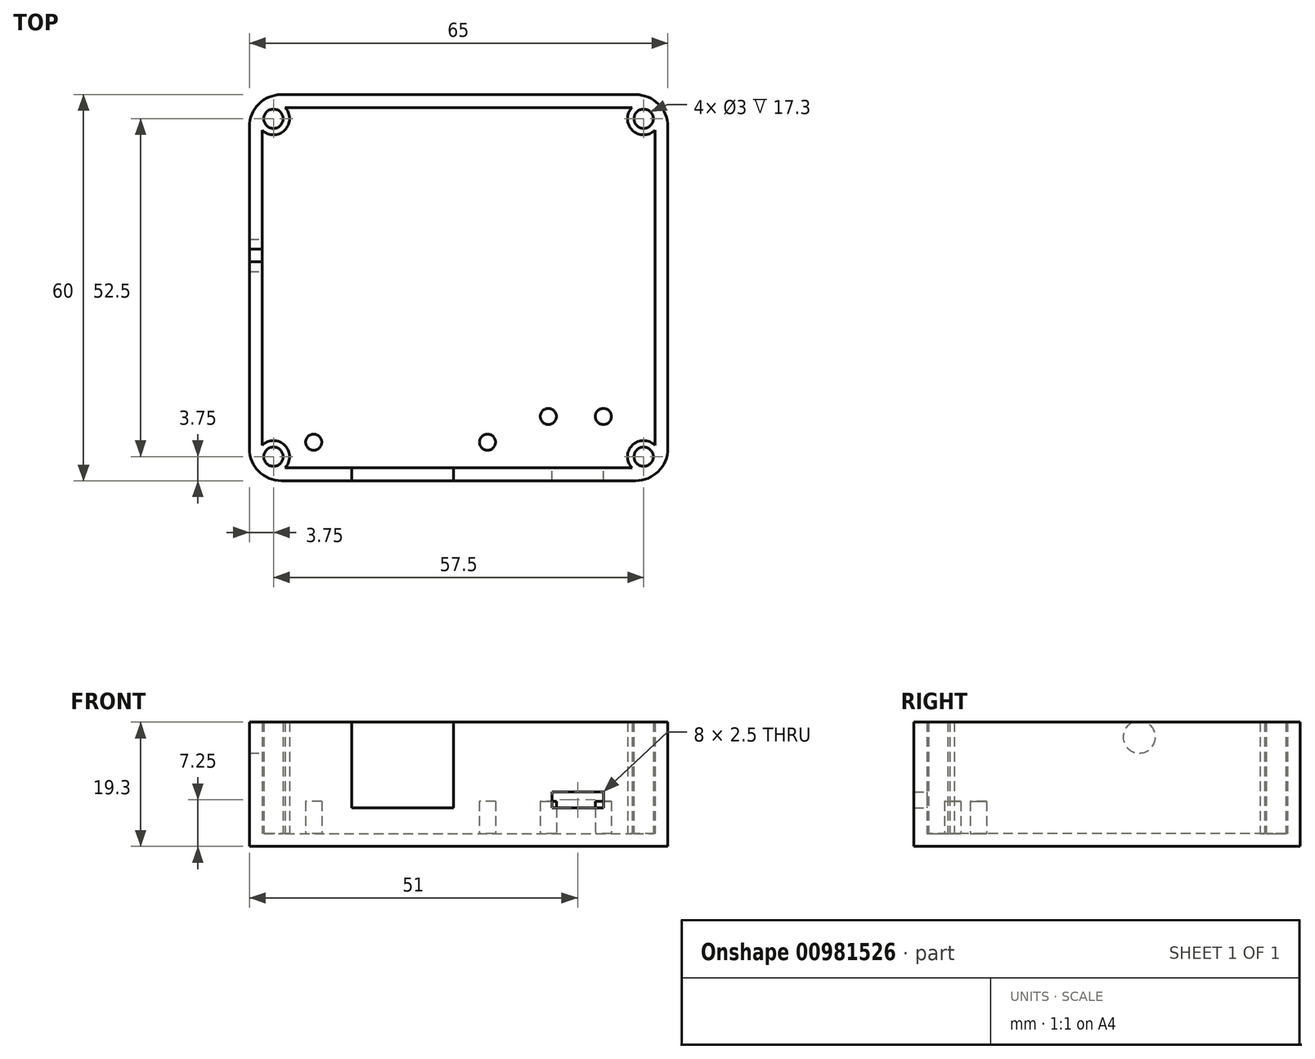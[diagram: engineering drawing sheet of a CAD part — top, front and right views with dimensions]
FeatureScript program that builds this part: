
annotation { "Feature Type Name" : "Feature", "Feature Type Description" : "" }
export const myFeature = defineFeature(function(context is Context, id is Id, definition is map)
    precondition{}
    {
        {
            var Q0;
            Q0=qCreatedBy(makeId("Top.planeOp"),FACE);
            var sketch = newSketch(context, id + "F0", { "sketchPlane" : qUnion([Q0])});
            skLineSegment(sketch, "E0.bottom", {"start": v(-32.5, -30) * mm, "end": v(32.5, -30) * mm});
            skLineSegment(sketch, "E0.top", {"start": v(-32.5, 30) * mm, "end": v(32.5, 30) * mm});
            skLineSegment(sketch, "E0.left", {"start": v(-32.5, -30) * mm, "end": v(-32.5, 30) * mm});
            skLineSegment(sketch, "E0.right", {"start": v(32.5, -30) * mm, "end": v(32.5, 30) * mm});
            skPoint(sketch, "E0.middle", {"position": v(0, 0) * mm});
            skCircle(sketch, "E1", {"center": v(22.5, -20) * mm, "radius": 1.25 * mm});
            skCircle(sketch, "E2", {"center": v(13.95, -20) * mm, "radius": 1.25 * mm});
            skCircle(sketch, "E3", {"center": v(-22.5, -24) * mm, "radius": 1.25 * mm});
            skCircle(sketch, "E4", {"center": v(4.5, -24) * mm, "radius": 1.25 * mm});
            skLineSegment(sketch, "E5.bottom", {"start": v(-30.5, 28) * mm, "end": v(30.5, 28) * mm});
            skLineSegment(sketch, "E5.top", {"start": v(-30.5, -28) * mm, "end": v(30.5, -28) * mm});
            skLineSegment(sketch, "E5.left", {"start": v(-30.5, 28) * mm, "end": v(-30.5, -28) * mm});
            skLineSegment(sketch, "E5.right", {"start": v(30.5, 28) * mm, "end": v(30.5, -28) * mm});
            skCircle(sketch, "E6", {"center": v(-28.75, 26.25) * mm, "radius": 2.5 * mm});
            skCircle(sketch, "E7", {"center": v(28.75, 26.25) * mm, "radius": 2.5 * mm});
            skCircle(sketch, "E8", {"center": v(28.75, -26.25) * mm, "radius": 2.5 * mm});
            skCircle(sketch, "E9", {"center": v(-28.75, -26.25) * mm, "radius": 2.5 * mm});
            skSolve(sketch);
        }
        {
            var Q0;
            Q0=makeQuery(id+"F0.imprint","IMPRINT",FACE,{"disambiguationData":[TD([[makeQuery(id+"F0.imprint","IMPRINT",EDGE,{"derivedFrom":sQuery(id+"F0.wireOp",EDGE,"E0.bottom")}),1.0]])]});
            extrude(context, id + "F1", {"entities" : qUnion([Q0]), "depth" : 17.3 * mm, "offsetDistance" : 25 * mm});
        }
        {
            var Q0;
            Q0=qCreatedBy(makeId("Front.planeOp"),FACE);
            var sketch = newSketch(context, id + "F2", { "sketchPlane" : qUnion([Q0])});
            skLineSegment(sketch, "E10.bottom", {"start": v(-16.6, 17.3) * mm, "end": v(-0.8, 17.3) * mm});
            skLineSegment(sketch, "E10.top", {"start": v(-16.6, 4) * mm, "end": v(-0.8, 4) * mm});
            skLineSegment(sketch, "E10.left", {"start": v(-16.6, 17.3) * mm, "end": v(-16.6, 4) * mm});
            skLineSegment(sketch, "E10.right", {"start": v(-0.8, 17.3) * mm, "end": v(-0.8, 4) * mm});
            skPoint(sketch, "E10.middle", {"position": v(-8.7, 10.65) * mm});
            skLineSegment(sketch, "E11.bottom", {"start": v(14.5, 6.5) * mm, "end": v(22.5, 6.5) * mm});
            skLineSegment(sketch, "E11.top", {"start": v(14.5, 4) * mm, "end": v(22.5, 4) * mm});
            skLineSegment(sketch, "E11.left", {"start": v(14.5, 6.5) * mm, "end": v(14.5, 4) * mm});
            skLineSegment(sketch, "E11.right", {"start": v(22.5, 6.5) * mm, "end": v(22.5, 4) * mm});
            skPoint(sketch, "E11.middle", {"position": v(18.5, 5.25) * mm});
            skSolve(sketch);
        }
        {
            var Q0;
            Q0=makeQuery(id+"F2.imprint","IMPRINT",FACE,{"disambiguationData":[TD([[makeQuery(id+"F2.imprint","IMPRINT",EDGE,{"derivedFrom":sQuery(id+"F2.wireOp",EDGE,"E10.bottom")}),-1.0]])]});
            extrude(context, id + "F3", {"entities" : qUnion([Q0]), "operationType" : NewBodyOperationType.REMOVE, "depth" : 27.5 * mm, "offsetDistance" : 25 * mm, "hasSecondDirection" : true, "secondDirectionOppositeDirection" : false, "secondDirectionDepth" : 25 * mm});
        }
        {
            var Q0;
            Q0=qCreatedBy(makeId("Right.planeOp"),FACE);
            var sketch = newSketch(context, id + "F4", { "sketchPlane" : qUnion([Q0])});
            skCircle(sketch, "E12", {"center": v(5, 15) * mm, "radius": 4 * mm});
            skSolve(sketch);
        }
        {
            var Q0;
            Q0=sQuery(id+"F4.wireOp",VERTEX,"E12.center");
            var Q1;
            Q1=makeQuery(id+"F1.opExtrude","SWEPT_BODY",BODY,{"disambiguationData":[OSD([sQuery(id+"F0.wireOp",EDGE,"E0.bottom"),sQuery(id+"F0.wireOp",EDGE,"E0.top"),sQuery(id+"F0.wireOp",EDGE,"E0.left"),sQuery(id+"F0.wireOp",EDGE,"E0.right")])]});
            hole(context, id + "F5", {"style" : HoleStyle.SIMPLE, "endStyle" : HoleEndStyle.THROUGH, "holeDiameter" : 5 * mm, "majorDiameter" : 5 * mm, "isTappedThrough" : true, "tappedDepth" : 12 * mm, "tapClearance" : 3, "locations" : qUnion([Q0]), "scope" : qUnion([Q1])});
        }
        {
            var Q0;
            Q0=makeQuery(id+"F2.imprint","IMPRINT",FACE,{"disambiguationData":[TD([[makeQuery(id+"F2.imprint","IMPRINT",EDGE,{"derivedFrom":sQuery(id+"F2.wireOp",EDGE,"E11.bottom")}),-1.0]])]});
            extrude(context, id + "F6", {"entities" : qUnion([Q0]), "operationType" : NewBodyOperationType.REMOVE, "depth" : 30 * mm, "offsetDistance" : 25 * mm});
        }
        {
            var Q0;
            Q0=makeQuery(id+"F0.imprint","IMPRINT",FACE,{"disambiguationData":[TD([[makeQuery(id+"F0.imprint","IMPRINT",EDGE,{"derivedFrom":sQuery(id+"F0.wireOp",EDGE,"E1")}),-1.0]])]});
            var Q1;
            {var subQ0=sQuery(id+"F0.wireOp",EDGE,"E5.left");var subQ1=sQuery(id+"F0.wireOp",EDGE,"E3");var subQ2=makeQuery(id+"F0.imprint","INTERSECT",VERTEX,{"disambiguationData":[OD(0.0)],"derivedFrom":[subQ1,subQ0]});Q1=makeQuery(id+"F0.imprint","IMPRINT",FACE,{"disambiguationData":[TD([[makeQuery(id+"F0.imprint","IMPRINT",EDGE,{"disambiguationData":[TD([[subQ2,1.0]])],"derivedFrom":subQ1}),1.0]])]});}
            var Q2;
            Q2=makeQuery(id+"F0.imprint","IMPRINT",FACE,{"disambiguationData":[TD([[makeQuery(id+"F0.imprint","IMPRINT",EDGE,{"derivedFrom":sQuery(id+"F0.wireOp",EDGE,"E4")}),1.0]])]});
            var Q3;
            Q3=makeQuery(id+"F0.imprint","IMPRINT",FACE,{"disambiguationData":[TD([[makeQuery(id+"F0.imprint","IMPRINT",EDGE,{"derivedFrom":sQuery(id+"F0.wireOp",EDGE,"E2")}),1.0]])]});
            var Q4;
            Q4=makeQuery(id+"F0.imprint","IMPRINT",FACE,{"disambiguationData":[TD([[makeQuery(id+"F0.imprint","IMPRINT",EDGE,{"derivedFrom":sQuery(id+"F0.wireOp",EDGE,"E1")}),1.0]])]});
            var Q5;
            {var subQ0=sQuery(id+"F0.wireOp",EDGE,"E5.left");var subQ1=sQuery(id+"F0.wireOp",EDGE,"E5.bottom");var subQ2=makeQuery(id+"F0.imprint","INTERSECT",VERTEX,{"derivedFrom":[subQ1,subQ0]});Q5=makeQuery(id+"F0.imprint","IMPRINT",FACE,{"disambiguationData":[TD([[makeQuery(id+"F0.imprint","IMPRINT",EDGE,{"disambiguationData":[TD([[subQ2,-1.0]])],"derivedFrom":subQ1}),-1.0]])]});}
            var Q6;
            {var subQ0=sQuery(id+"F0.wireOp",EDGE,"E5.right");var subQ1=sQuery(id+"F0.wireOp",EDGE,"E5.bottom");var subQ2=makeQuery(id+"F0.imprint","INTERSECT",VERTEX,{"derivedFrom":[subQ1,subQ0]});Q6=makeQuery(id+"F0.imprint","IMPRINT",FACE,{"disambiguationData":[TD([[makeQuery(id+"F0.imprint","IMPRINT",EDGE,{"disambiguationData":[TD([[subQ2,1.0]])],"derivedFrom":subQ1}),-1.0]])]});}
            var Q7;
            Q7=makeQuery(id+"F0.imprint","IMPRINT",FACE,{"disambiguationData":[TD([[makeQuery(id+"F0.imprint","IMPRINT",EDGE,{"derivedFrom":sQuery(id+"F0.wireOp",EDGE,"E3")}),-1.0]])]});
            var Q8;
            {var subQ0=sQuery(id+"F0.wireOp",EDGE,"E5.right");var subQ1=sQuery(id+"F0.wireOp",EDGE,"E5.top");var subQ2=makeQuery(id+"F0.imprint","INTERSECT",VERTEX,{"derivedFrom":[subQ1,subQ0]});Q8=makeQuery(id+"F0.imprint","IMPRINT",FACE,{"disambiguationData":[TD([[makeQuery(id+"F0.imprint","IMPRINT",EDGE,{"disambiguationData":[TD([[subQ2,1.0]])],"derivedFrom":subQ1}),1.0]])]});}
            var Q9;
            {var subQ0=sQuery(id+"F0.wireOp",EDGE,"E5.right");var subQ1=sQuery(id+"F0.wireOp",EDGE,"E5.top");var subQ2=makeQuery(id+"F0.imprint","INTERSECT",VERTEX,{"derivedFrom":[subQ1,subQ0]});Q9=makeQuery(id+"F0.imprint","IMPRINT",FACE,{"disambiguationData":[TD([[makeQuery(id+"F0.imprint","IMPRINT",EDGE,{"disambiguationData":[TD([[subQ2,1.0]])],"derivedFrom":subQ1}),-1.0]])]});}
            var Q10;
            {var subQ0=sQuery(id+"F0.wireOp",EDGE,"E5.left");var subQ1=sQuery(id+"F0.wireOp",EDGE,"E5.top");var subQ2=makeQuery(id+"F0.imprint","INTERSECT",VERTEX,{"derivedFrom":[subQ1,subQ0]});Q10=makeQuery(id+"F0.imprint","IMPRINT",FACE,{"disambiguationData":[TD([[makeQuery(id+"F0.imprint","IMPRINT",EDGE,{"disambiguationData":[TD([[subQ2,-1.0]])],"derivedFrom":subQ1}),-1.0]])]});}
            var Q11;
            {var subQ0=sQuery(id+"F0.wireOp",EDGE,"E5.left");var subQ1=sQuery(id+"F0.wireOp",EDGE,"E5.bottom");var subQ2=makeQuery(id+"F0.imprint","INTERSECT",VERTEX,{"derivedFrom":[subQ1,subQ0]});Q11=makeQuery(id+"F0.imprint","IMPRINT",FACE,{"disambiguationData":[TD([[makeQuery(id+"F0.imprint","IMPRINT",EDGE,{"disambiguationData":[TD([[subQ2,-1.0]])],"derivedFrom":subQ1}),1.0]])]});}
            var Q12;
            {var subQ0=sQuery(id+"F0.wireOp",EDGE,"E5.right");var subQ1=sQuery(id+"F0.wireOp",EDGE,"E5.bottom");var subQ2=makeQuery(id+"F0.imprint","INTERSECT",VERTEX,{"derivedFrom":[subQ1,subQ0]});Q12=makeQuery(id+"F0.imprint","IMPRINT",FACE,{"disambiguationData":[TD([[makeQuery(id+"F0.imprint","IMPRINT",EDGE,{"disambiguationData":[TD([[subQ2,1.0]])],"derivedFrom":subQ1}),1.0]])]});}
            var Q13;
            Q13=makeQuery(id+"F0.imprint","IMPRINT",FACE,{"disambiguationData":[TD([[makeQuery(id+"F0.imprint","IMPRINT",EDGE,{"derivedFrom":sQuery(id+"F0.wireOp",EDGE,"E0.bottom")}),1.0]])]});
            var Q14;
            {var subQ0=sQuery(id+"F0.wireOp",EDGE,"E5.left");var subQ1=sQuery(id+"F0.wireOp",EDGE,"E5.top");var subQ2=makeQuery(id+"F0.imprint","INTERSECT",VERTEX,{"derivedFrom":[subQ1,subQ0]});Q14=makeQuery(id+"F0.imprint","IMPRINT",FACE,{"disambiguationData":[TD([[makeQuery(id+"F0.imprint","IMPRINT",EDGE,{"disambiguationData":[TD([[subQ2,-1.0]])],"derivedFrom":subQ1}),1.0]])]});}
            extrude(context, id + "F7", {"entities" : qUnion([Q0, Q1, Q2, Q3, Q4, Q5, Q6, Q7, Q8, Q9, Q10, Q11, Q12, Q13, Q14]), "operationType" : NewBodyOperationType.ADD, "oppositeDirection" : true, "depth" : 2 * mm, "offsetDistance" : 25 * mm});
        }
        {
            var Q0;
            Q0=makeQuery(id+"F0.imprint","IMPRINT",FACE,{"disambiguationData":[TD([[makeQuery(id+"F0.imprint","IMPRINT",EDGE,{"derivedFrom":sQuery(id+"F0.wireOp",EDGE,"E1")}),1.0]])]});
            var Q1;
            Q1=makeQuery(id+"F0.imprint","IMPRINT",FACE,{"disambiguationData":[TD([[makeQuery(id+"F0.imprint","IMPRINT",EDGE,{"derivedFrom":sQuery(id+"F0.wireOp",EDGE,"E2")}),1.0]])]});
            var Q2;
            Q2=makeQuery(id+"F0.imprint","IMPRINT",FACE,{"disambiguationData":[TD([[makeQuery(id+"F0.imprint","IMPRINT",EDGE,{"derivedFrom":sQuery(id+"F0.wireOp",EDGE,"E4")}),1.0]])]});
            var Q3;
            {var subQ0=sQuery(id+"F0.wireOp",EDGE,"E5.left");var subQ1=sQuery(id+"F0.wireOp",EDGE,"E3");var subQ2=makeQuery(id+"F0.imprint","INTERSECT",VERTEX,{"disambiguationData":[OD(0.0)],"derivedFrom":[subQ1,subQ0]});Q3=makeQuery(id+"F0.imprint","IMPRINT",FACE,{"disambiguationData":[TD([[makeQuery(id+"F0.imprint","IMPRINT",EDGE,{"disambiguationData":[TD([[subQ2,1.0]])],"derivedFrom":subQ1}),1.0]])]});}
            extrude(context, id + "F8", {"entities" : qUnion([Q0, Q1, Q2, Q3]), "operationType" : NewBodyOperationType.ADD, "depth" : 5 * mm, "offsetDistance" : 25 * mm});
        }
        {
            var Q0;
            {var subQ0=sQuery(id+"F0.wireOp",EDGE,"E5.right");var subQ1=sQuery(id+"F0.wireOp",EDGE,"E5.top");var subQ2=makeQuery(id+"F0.imprint","INTERSECT",VERTEX,{"derivedFrom":[subQ1,subQ0]});Q0=makeQuery(id+"F0.imprint","IMPRINT",FACE,{"disambiguationData":[TD([[makeQuery(id+"F0.imprint","IMPRINT",EDGE,{"disambiguationData":[TD([[subQ2,1.0]])],"derivedFrom":subQ1}),1.0]])]});}
            var Q1;
            {var subQ0=sQuery(id+"F0.wireOp",EDGE,"E5.right");var subQ1=sQuery(id+"F0.wireOp",EDGE,"E5.top");var subQ2=makeQuery(id+"F0.imprint","INTERSECT",VERTEX,{"derivedFrom":[subQ1,subQ0]});Q1=makeQuery(id+"F0.imprint","IMPRINT",FACE,{"disambiguationData":[TD([[makeQuery(id+"F0.imprint","IMPRINT",EDGE,{"disambiguationData":[TD([[subQ2,1.0]])],"derivedFrom":subQ1}),-1.0]])]});}
            var Q2;
            {var subQ0=sQuery(id+"F0.wireOp",EDGE,"E5.right");var subQ1=sQuery(id+"F0.wireOp",EDGE,"E5.bottom");var subQ2=makeQuery(id+"F0.imprint","INTERSECT",VERTEX,{"derivedFrom":[subQ1,subQ0]});Q2=makeQuery(id+"F0.imprint","IMPRINT",FACE,{"disambiguationData":[TD([[makeQuery(id+"F0.imprint","IMPRINT",EDGE,{"disambiguationData":[TD([[subQ2,1.0]])],"derivedFrom":subQ1}),1.0]])]});}
            var Q3;
            {var subQ0=sQuery(id+"F0.wireOp",EDGE,"E5.right");var subQ1=sQuery(id+"F0.wireOp",EDGE,"E5.bottom");var subQ2=makeQuery(id+"F0.imprint","INTERSECT",VERTEX,{"derivedFrom":[subQ1,subQ0]});Q3=makeQuery(id+"F0.imprint","IMPRINT",FACE,{"disambiguationData":[TD([[makeQuery(id+"F0.imprint","IMPRINT",EDGE,{"disambiguationData":[TD([[subQ2,1.0]])],"derivedFrom":subQ1}),-1.0]])]});}
            var Q4;
            {var subQ0=sQuery(id+"F0.wireOp",EDGE,"E5.left");var subQ1=sQuery(id+"F0.wireOp",EDGE,"E5.bottom");var subQ2=makeQuery(id+"F0.imprint","INTERSECT",VERTEX,{"derivedFrom":[subQ1,subQ0]});Q4=makeQuery(id+"F0.imprint","IMPRINT",FACE,{"disambiguationData":[TD([[makeQuery(id+"F0.imprint","IMPRINT",EDGE,{"disambiguationData":[TD([[subQ2,-1.0]])],"derivedFrom":subQ1}),-1.0]])]});}
            var Q5;
            {var subQ0=sQuery(id+"F0.wireOp",EDGE,"E5.left");var subQ1=sQuery(id+"F0.wireOp",EDGE,"E5.bottom");var subQ2=makeQuery(id+"F0.imprint","INTERSECT",VERTEX,{"derivedFrom":[subQ1,subQ0]});Q5=makeQuery(id+"F0.imprint","IMPRINT",FACE,{"disambiguationData":[TD([[makeQuery(id+"F0.imprint","IMPRINT",EDGE,{"disambiguationData":[TD([[subQ2,-1.0]])],"derivedFrom":subQ1}),1.0]])]});}
            var Q6;
            {var subQ0=sQuery(id+"F0.wireOp",EDGE,"E5.left");var subQ1=sQuery(id+"F0.wireOp",EDGE,"E5.top");var subQ2=makeQuery(id+"F0.imprint","INTERSECT",VERTEX,{"derivedFrom":[subQ1,subQ0]});Q6=makeQuery(id+"F0.imprint","IMPRINT",FACE,{"disambiguationData":[TD([[makeQuery(id+"F0.imprint","IMPRINT",EDGE,{"disambiguationData":[TD([[subQ2,-1.0]])],"derivedFrom":subQ1}),-1.0]])]});}
            var Q7;
            {var subQ0=sQuery(id+"F0.wireOp",EDGE,"E5.left");var subQ1=sQuery(id+"F0.wireOp",EDGE,"E5.top");var subQ2=makeQuery(id+"F0.imprint","INTERSECT",VERTEX,{"derivedFrom":[subQ1,subQ0]});Q7=makeQuery(id+"F0.imprint","IMPRINT",FACE,{"disambiguationData":[TD([[makeQuery(id+"F0.imprint","IMPRINT",EDGE,{"disambiguationData":[TD([[subQ2,-1.0]])],"derivedFrom":subQ1}),1.0]])]});}
            extrude(context, id + "F9", {"entities" : qUnion([Q0, Q1, Q2, Q3, Q4, Q5, Q6, Q7]), "operationType" : NewBodyOperationType.ADD, "depth" : 17.3 * mm, "offsetDistance" : 25 * mm, "hasSecondDirection" : true, "secondDirectionOppositeDirection" : false, "secondDirectionDepth" : 0 * mm});
        }
        {
            var Q0;
            Q0=sQuery(id+"F0.wireOp",VERTEX,"E6.center");
            var Q1;
            Q1=sQuery(id+"F0.wireOp",VERTEX,"E7.center");
            var Q2;
            Q2=sQuery(id+"F0.wireOp",VERTEX,"E8.center");
            var Q3;
            Q3=sQuery(id+"F0.wireOp",VERTEX,"E9.center");
            var Q4;
            Q4=makeQuery(id+"F1.opExtrude","SWEPT_BODY",BODY,{"disambiguationData":[OSD([sQuery(id+"F0.wireOp",EDGE,"E0.bottom"),sQuery(id+"F0.wireOp",EDGE,"E0.top"),sQuery(id+"F0.wireOp",EDGE,"E0.left"),sQuery(id+"F0.wireOp",EDGE,"E0.right"),sQuery(id+"F0.wireOp",EDGE,"E5.bottom"),sQuery(id+"F0.wireOp",EDGE,"E5.top"),sQuery(id+"F0.wireOp",EDGE,"E5.left"),sQuery(id+"F0.wireOp",EDGE,"E5.right"),sQuery(id+"F0.wireOp",EDGE,"E6"),sQuery(id+"F0.wireOp",EDGE,"E7"),sQuery(id+"F0.wireOp",EDGE,"E8"),sQuery(id+"F0.wireOp",EDGE,"E9")])]});
            hole(context, id + "F10", {"style" : HoleStyle.SIMPLE, "endStyle" : HoleEndStyle.BLIND, "oppositeDirection" : true, "holeDiameter" : 3 * mm, "majorDiameter" : 5 * mm, "holeDepth" : 22 * mm, "isTappedThrough" : true, "tappedDepth" : 12 * mm, "tapClearance" : 3, "locations" : qUnion([Q0, Q1, Q2, Q3]), "scope" : qUnion([Q4])});
        }
        {
            var Q0;
            Q0=makeQuery(id+"F2.imprint","IMPRINT",FACE,{"disambiguationData":[TD([[makeQuery(id+"F2.imprint","IMPRINT",EDGE,{"derivedFrom":sQuery(id+"F2.wireOp",EDGE,"E10.bottom")}),-1.0]])]});
            extrude(context, id + "F11", {"entities" : qUnion([Q0]), "operationType" : NewBodyOperationType.REMOVE, "depth" : 30 * mm, "offsetDistance" : 25 * mm});
        }
        {
            var Q0;
            {var subQ0=sQuery(id+"F0.wireOp",EDGE,"E0.right");var subQ1=sQuery(id+"F0.wireOp",EDGE,"E0.bottom");Q0=makeQuery(id+"F7.boolean.opBoolean","MERGE",EDGE,{"derivedFrom":[makeQuery(id+"F1.opExtrude","SWEPT_EDGE",EDGE,{"disambiguationData":[OSD([subQ1,subQ0])]}),makeQuery(id+"F7.opExtrude","SWEPT_EDGE",EDGE,{"disambiguationData":[OSD([subQ1,subQ0])]})]});}
            var Q1;
            {var subQ0=sQuery(id+"F0.wireOp",EDGE,"E0.right");var subQ1=sQuery(id+"F0.wireOp",EDGE,"E0.top");Q1=makeQuery(id+"F7.boolean.opBoolean","MERGE",EDGE,{"derivedFrom":[makeQuery(id+"F1.opExtrude","SWEPT_EDGE",EDGE,{"disambiguationData":[OSD([subQ1,subQ0])]}),makeQuery(id+"F7.opExtrude","SWEPT_EDGE",EDGE,{"disambiguationData":[OSD([subQ1,subQ0])]})]});}
            var Q2;
            {var subQ0=sQuery(id+"F0.wireOp",EDGE,"E0.left");var subQ1=sQuery(id+"F0.wireOp",EDGE,"E0.top");Q2=makeQuery(id+"F7.boolean.opBoolean","MERGE",EDGE,{"derivedFrom":[makeQuery(id+"F1.opExtrude","SWEPT_EDGE",EDGE,{"disambiguationData":[OSD([subQ1,subQ0])]}),makeQuery(id+"F7.opExtrude","SWEPT_EDGE",EDGE,{"disambiguationData":[OSD([subQ1,subQ0])]})]});}
            var Q3;
            {var subQ0=sQuery(id+"F0.wireOp",EDGE,"E0.left");var subQ1=sQuery(id+"F0.wireOp",EDGE,"E0.bottom");Q3=makeQuery(id+"F7.boolean.opBoolean","MERGE",EDGE,{"derivedFrom":[makeQuery(id+"F1.opExtrude","SWEPT_EDGE",EDGE,{"disambiguationData":[OSD([subQ1,subQ0])]}),makeQuery(id+"F7.opExtrude","SWEPT_EDGE",EDGE,{"disambiguationData":[OSD([subQ1,subQ0])]})]});}
            fillet(context, id + "F12", {"entities" : qUnion([Q0, Q1, Q2, Q3]), "radius" : 5 * mm, "tangentPropagation" : true, "allowEdgeOverflow" : false});
        }
    });
